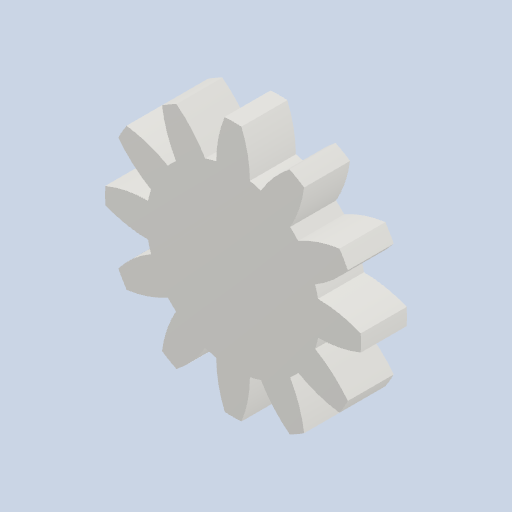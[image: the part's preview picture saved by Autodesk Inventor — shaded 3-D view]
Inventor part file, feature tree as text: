
AUTODESK INVENTOR PART (.ipt)
format: ipt  version: 2022 (Build 260153000, 153)  size: 188,416 bytes
history: native  units: mm (DEFAULTED — no unit token found)
features: plane x3, other x3, sketch x2, extrude x1
ambient origin geometry x8: Origin, YZ Plane, XZ Plane, XY Plane, X Axis, Y Axis, Z Axis, Center Point
bodies: Solid1 (feature_tree)
feature tree (9):
  extrude  "Extrusion1"  Depth=5.0mm TaperAngle=0.0deg
  plane  "Work Plane2"
  plane  "Work Plane8"
  plane  "Work Plane9"
  other  "Цилиндрическое зубчатое зацепление"
  sketch  "Sketch1"  dims[d0=27.891697mm d1=5.0mm d2=0.0mm]
  sketch  "Sketch2"  dims[d3=24.0mm d4=10.0mm d5=0.0mm d16=40.945848mm d17=0.0mm d34=15.0deg d39=0.0mm d41=0.0mm d43=40.945848mm d46=40.945848mm d47=0.0mm d48=0.0mm]
  other  "Srf1"
  other  "Средний диаметр"
